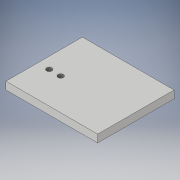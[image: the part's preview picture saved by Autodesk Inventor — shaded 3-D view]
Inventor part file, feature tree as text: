
AUTODESK INVENTOR PART (.ipt)
format: ipt  version: 2019 (Build 230136000, 136)  size: 107,008 bytes
history: native  units: mm
features: extrude x2, thread x2, sketch x2
ambient origin geometry x8: Origin, YZ Plane, XZ Plane, XY Plane, X Axis, Y Axis, Z Axis, Center Point
bodies: Solid1 (feature_tree)
feature tree (6):
  extrude  "Extrusion1"  Depth=120.0mm
  extrude  "Extrusion2"  Depth=10.0mm
  thread  "Thread1"  [1 undecoded]
  thread  "Thread2"  [1 undecoded]
  sketch  "Sketch1"  dims[d0=100.0mm d1=120.0mm]
  sketch  "Sketch2"  dims[d2=70.0mm d3=41.666667mm d4=10.0mm d5=0.0mm d6=7.0mm d7=7.0mm d8=30.0mm d9=15.0mm d12=15.0mm d13=40.0mm d14=5.0mm d15=0.0mm d16=10.0mm d17=0.0mm d18=10.0mm d19=0.0mm]
note: 2 required parameter values undecoded (feature->parameter linkage not recoverable at this tier; creation-order binding heuristic only, values carry confidence <= 0.55)
